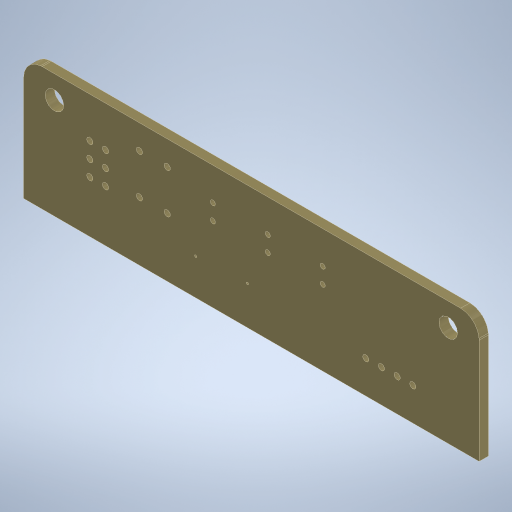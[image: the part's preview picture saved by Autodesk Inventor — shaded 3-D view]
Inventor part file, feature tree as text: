
AUTODESK INVENTOR PART (.ipt)
format: ipt  version: 2023 (Build 270158000, 158)  size: 397,312 bytes
history: native  units: in
note: dims shown in document units (in); Inventor stores cm internally (conversion verified against a paired STEP export)
features: other x2, extrude x1, sketch x1, projected_geometry x1
ambient origin geometry x8: Origin, YZ Plane, XZ Plane, XY Plane, X Axis, Y Axis, Z Axis, Center Point
bodies: Body1 (feature_tree)
feature tree (5):
  other  "Bryła1"
  extrude  "Wyciągnięcie proste2"  TaperAngle=0.0deg  [1 undecoded]
  sketch  "Szkic3"
  projected_geometry  "Pętla rzutowana2"
  other  "Płytka"
note: 1 required parameter value undecoded (feature->parameter linkage not recoverable at this tier; creation-order binding heuristic only, values carry confidence <= 0.55)
